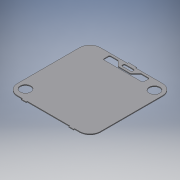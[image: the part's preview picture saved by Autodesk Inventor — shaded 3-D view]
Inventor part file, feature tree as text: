
AUTODESK INVENTOR PART (.ipt)
format: ipt  version: 2016 SP2 (Build 200236200, 236)  size: 179,712 bytes
history: native  units: mm
features: reference x12, extrude x1, fillet x1, sketch x1
ambient origin geometry x8: Origin, YZ Plane, XZ Plane, XY Plane, X Axis, Y Axis, Z Axis, Center Point
bodies: Volumenkörper1 (feature_tree)
feature tree (15):
  extrude  "Extrusion1"  Depth=1.0mm
  fillet  "Rundung1"  Radius=0.3mm
  sketch  "Skizze1"  dims[d0=0.1mm d1=0.3mm d2=0.3mm d3=0.3mm d4=0.3mm d5=0.3mm d6=0.3mm d7=0.3mm d8=0.3mm d9=0.3mm d10=135.0deg d11=1.5mm d12=2.0mm d13=8.0mm d14=8.0mm d15=12.0mm d17=2.0mm d18=10.0mm d19=1.0mm d20=2.0mm d21=3.0mm d22=2.0mm d23=0.8mm d24=0.0mm d25=1.0mm d26=1.0mm d27=1.0mm]
  reference  "Referenz1"
  reference  "Referenz2"
  reference  "Referenz3"
  reference  "Referenz4"
  reference  "Referenz5"
  reference  "Referenz6"
  reference  "Referenz7"
  reference  "Referenz8"
  reference  "Referenz9"
  reference  "Referenz10"
  reference  "Referenz11"
  reference  "Referenz12"
